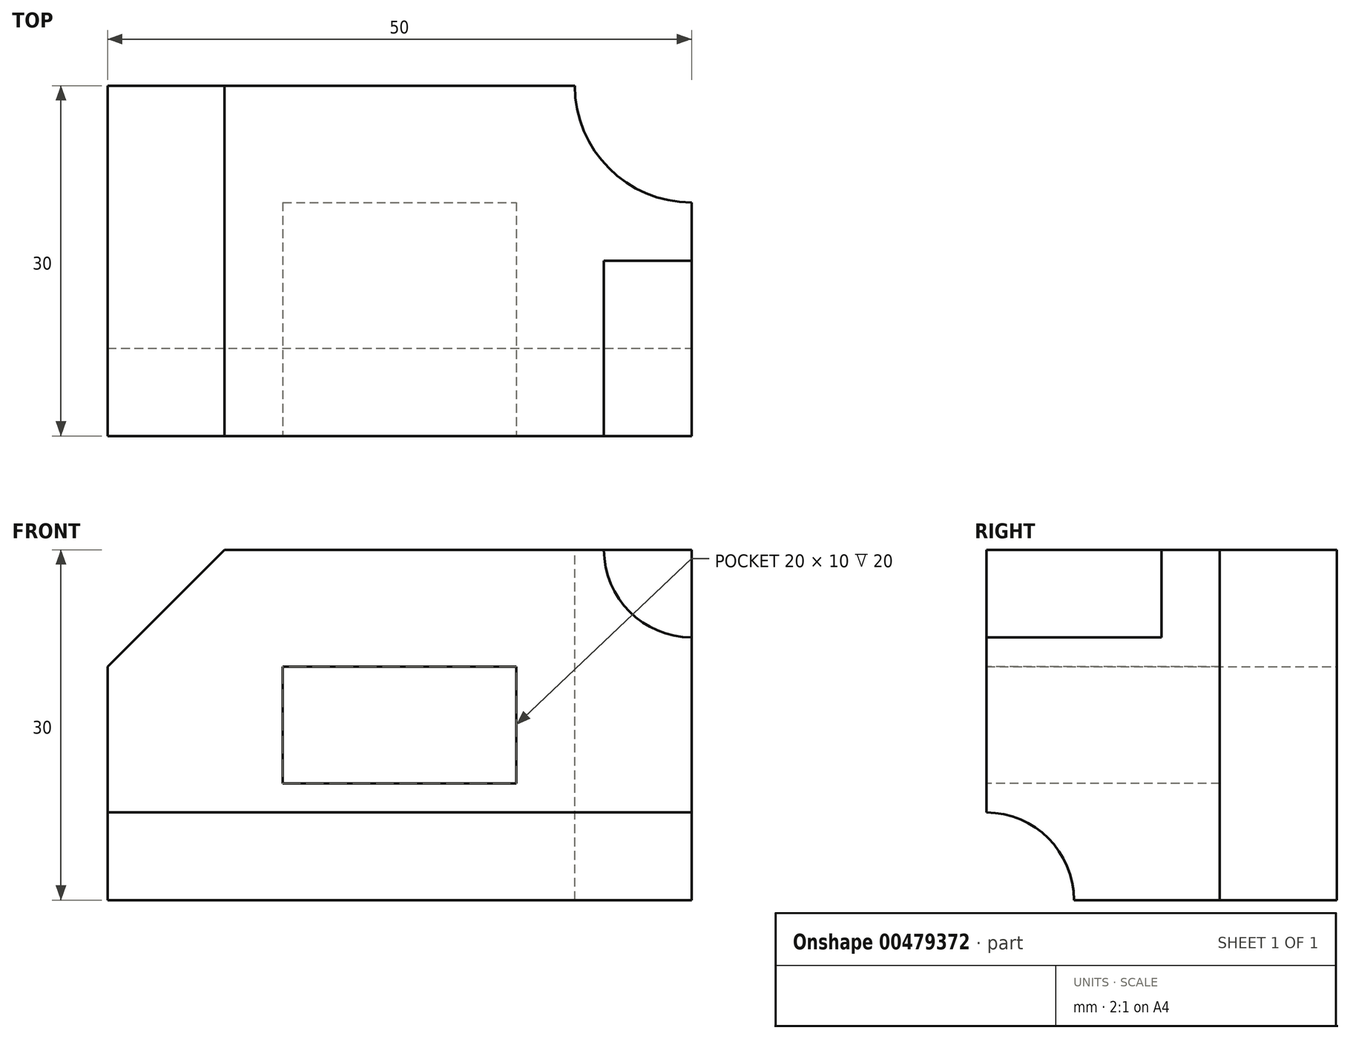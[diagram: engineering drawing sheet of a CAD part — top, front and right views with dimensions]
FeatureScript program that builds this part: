
annotation { "Feature Type Name" : "Feature", "Feature Type Description" : "" }
export const myFeature = defineFeature(function(context is Context, id is Id, definition is map)
    precondition{}
    {
        {
            var Q0;
            Q0=qCreatedBy(makeId("Front.planeOp"),FACE);
            var sketch = newSketch(context, id + "F0", { "sketchPlane" : qUnion([Q0])});
            skLineSegment(sketch, "E0.bottom", {"start": v(0, 0) * mm, "end": v(50, 0) * mm});
            skLineSegment(sketch, "E0.top", {"start": v(0, 30) * mm, "end": v(50, 30) * mm});
            skLineSegment(sketch, "E0.left", {"start": v(0, 0) * mm, "end": v(0, 30) * mm});
            skLineSegment(sketch, "E0.right", {"start": v(50, 0) * mm, "end": v(50, 30) * mm});
            skSolve(sketch);
        }
        {
            var Q0;
            Q0 = qSketchRegion(id + "F0", true);
            extrude(context, id + "F1", {"entities" : qUnion([Q0]), "depth" : 30 * mm});
        }
        {
            var Q0;
            Q0=makeQuery(id+"F1.opExtrude","SWEPT_EDGE",EDGE,{"disambiguationData":[OSD([sQuery(id+"F0.wireOp",EDGE,"E0.top"),sQuery(id+"F0.wireOp",EDGE,"E0.left")])]});
            chamfer(context, id + "F2", {"entities" : qUnion([Q0]), "width" : 10 * mm, "tangentPropagation" : true});
        }
        {
            var Q0;
            Q0=makeQuery(id+"F1.opExtrude","SWEPT_FACE",FACE,{"disambiguationData":[OSD([sQuery(id+"F0.wireOp",EDGE,"E0.right")])]});
            var sketch = newSketch(context, id + "F3", { "sketchPlane" : qUnion([Q0])});
            skCircle(sketch, "E1", {"center": v(-30, 0) * mm, "radius": 7.5 * mm});
            skSolve(sketch);
        }
        {
            var Q0;
            Q0 = qSketchRegion(id + "F3", true);
            extrude(context, id + "F4", {"entities" : qUnion([Q0]), "operationType" : NewBodyOperationType.REMOVE, "endBound" : BoundingType.THROUGH_ALL, "oppositeDirection" : true, "depth" : 25 * mm});
        }
        {
            var Q0;
            Q0=makeQuery(id+"F1.opExtrude","SWEPT_FACE",FACE,{"disambiguationData":[OSD([sQuery(id+"F0.wireOp",EDGE,"E0.top")])]});
            var sketch = newSketch(context, id + "F5", { "sketchPlane" : qUnion([Q0])});
            skCircle(sketch, "E2", {"center": v(50, 0) * mm, "radius": 10 * mm});
            skSolve(sketch);
        }
        {
            var Q0;
            Q0 = qSketchRegion(id + "F5", true);
            extrude(context, id + "F6", {"entities" : qUnion([Q0]), "operationType" : NewBodyOperationType.REMOVE, "endBound" : BoundingType.THROUGH_ALL, "oppositeDirection" : true, "depth" : 25 * mm});
        }
        {
            var Q0;
            Q0=makeQuery(id+"F1.opExtrude","CAP_FACE",FACE,{"disambiguationData":[OSD([sQuery(id+"F0.wireOp",EDGE,"E0.bottom"),sQuery(id+"F0.wireOp",EDGE,"E0.top"),sQuery(id+"F0.wireOp",EDGE,"E0.left"),sQuery(id+"F0.wireOp",EDGE,"E0.right")])],"isStart":false});
            var sketch = newSketch(context, id + "F7", { "sketchPlane" : qUnion([Q0])});
            skLineSegment(sketch, "E3.bottom", {"start": v(15, 20) * mm, "end": v(35, 20) * mm});
            skLineSegment(sketch, "E3.top", {"start": v(15, 10) * mm, "end": v(35, 10) * mm});
            skLineSegment(sketch, "E3.left", {"start": v(15, 20) * mm, "end": v(15, 10) * mm});
            skLineSegment(sketch, "E3.right", {"start": v(35, 20) * mm, "end": v(35, 10) * mm});
            skSolve(sketch);
        }
        {
            var Q0;
            Q0 = qSketchRegion(id + "F7", true);
            extrude(context, id + "F8", {"entities" : qUnion([Q0]), "operationType" : NewBodyOperationType.REMOVE, "oppositeDirection" : true, "depth" : 20 * mm});
        }
        {
            var Q0;
            Q0=makeQuery(id+"F1.opExtrude","CAP_FACE",FACE,{"disambiguationData":[OSD([sQuery(id+"F0.wireOp",EDGE,"E0.bottom"),sQuery(id+"F0.wireOp",EDGE,"E0.top"),sQuery(id+"F0.wireOp",EDGE,"E0.left"),sQuery(id+"F0.wireOp",EDGE,"E0.right")])],"isStart":false});
            var sketch = newSketch(context, id + "F9", { "sketchPlane" : qUnion([Q0])});
            skCircle(sketch, "E4", {"center": v(50, 30) * mm, "radius": 7.5 * mm});
            skSolve(sketch);
        }
        {
            var Q0;
            Q0 = qSketchRegion(id + "F9", true);
            extrude(context, id + "F10", {"entities" : qUnion([Q0]), "operationType" : NewBodyOperationType.REMOVE, "oppositeDirection" : true, "depth" : 15 * mm});
        }
    });
